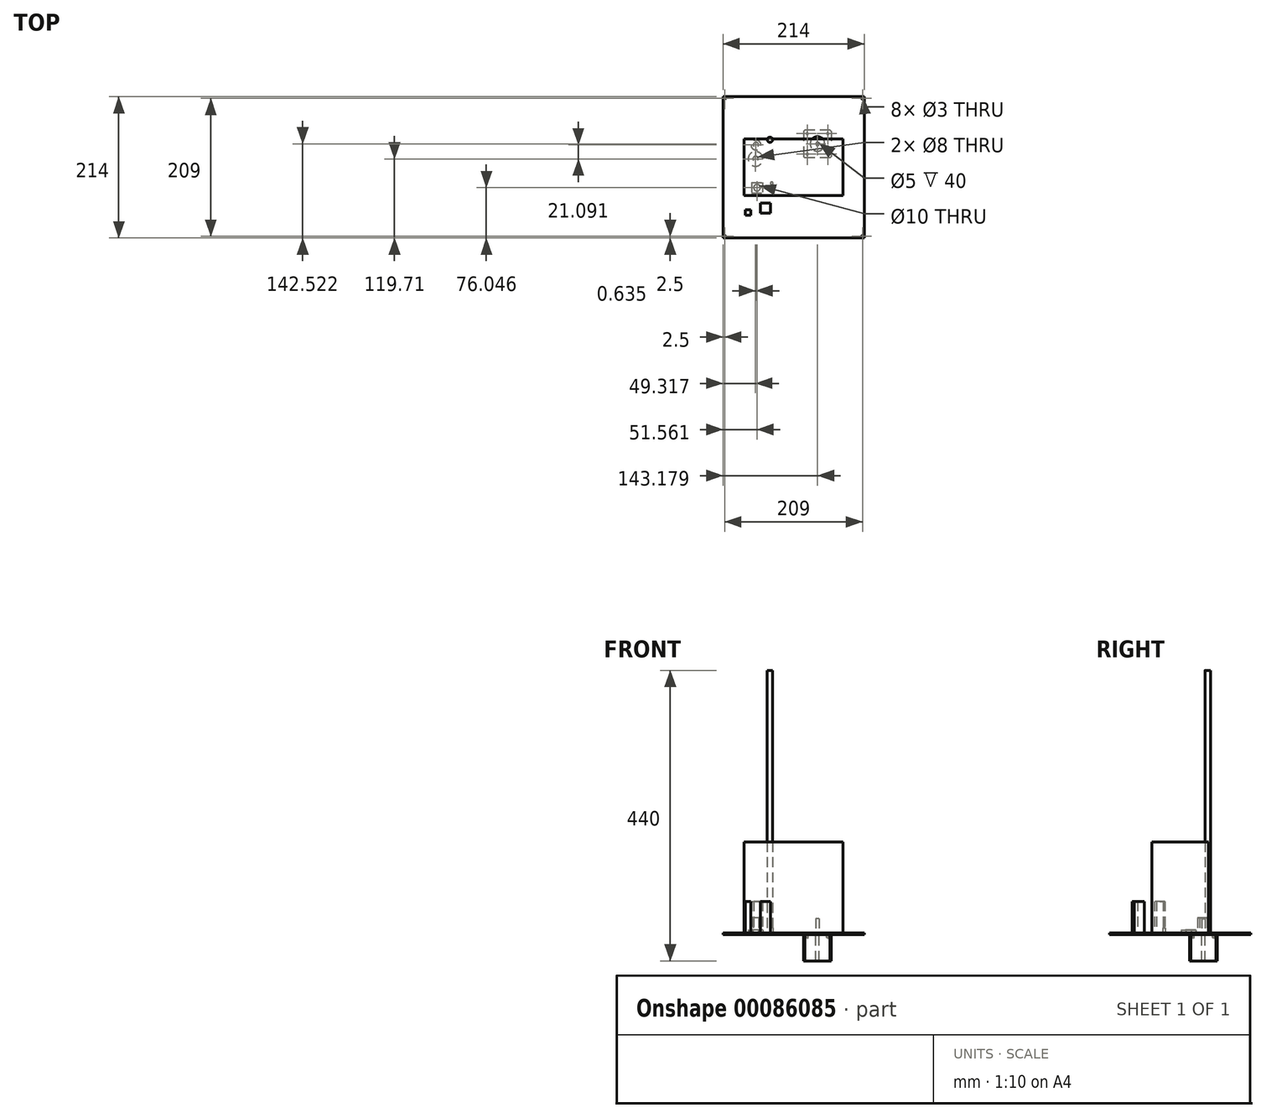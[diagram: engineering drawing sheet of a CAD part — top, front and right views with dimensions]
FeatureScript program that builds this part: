
annotation { "Feature Type Name" : "Feature", "Feature Type Description" : "" }
export const myFeature = defineFeature(function(context is Context, id is Id, definition is map)
    precondition{}
    {
        {
            var Q0;
            Q0=qCreatedBy(makeId("Top.planeOp"),FACE);
            var sketch = newSketch(context, id + "F0", { "sketchPlane" : qUnion([Q0])});
            skCircle(sketch, "E0", {"center": v(-57.05, 33.8) * mm, "radius": 4 * mm});
            skCircle(sketch, "E1", {"center": v(-57.05, 33.8) * mm, "radius": 7.5 * mm});
            skCircle(sketch, "E2", {"center": v(-35.88, 41.78) * mm, "radius": 4 * mm});
            skCircle(sketch, "E3", {"center": v(-57.68, 12.71) * mm, "radius": 11 * mm});
            skCircle(sketch, "E4", {"center": v(-57.68, 12.71) * mm, "radius": 4 * mm});
            skLineSegment(sketch, "E5.bottom", {"start": v(57.18, 56.52) * mm, "end": v(15.18, 56.52) * mm});
            skLineSegment(sketch, "E5.top", {"start": v(57.18, 14.52) * mm, "end": v(15.18, 14.52) * mm});
            skLineSegment(sketch, "E5.left", {"start": v(57.18, 56.52) * mm, "end": v(57.18, 14.52) * mm});
            skLineSegment(sketch, "E5.right", {"start": v(15.18, 56.52) * mm, "end": v(15.18, 14.52) * mm});
            skPoint(sketch, "E5.middle", {"position": v(36.18, 35.52) * mm});
            skCircle(sketch, "E6", {"center": v(36.18, 35.52) * mm, "radius": 11 * mm});
            skCircle(sketch, "E7", {"center": v(36.18, 35.52) * mm, "radius": 2.5 * mm});
            skLineSegment(sketch, "E8", {"start": v(36.18, 56.52) * mm, "end": v(36.18, 14.52) * mm, "construction": true});
            skLineSegment(sketch, "E9", {"start": v(57.18, 35.52) * mm, "end": v(15.18, 35.52) * mm, "construction": true});
            skPoint(sketch, "E10", {"position": v(20.68, 51.02) * mm});
            skPoint(sketch, "E11.MirrorP", {"position": v(51.68, 51.02) * mm});
            skPoint(sketch, "E12.MirrorP", {"position": v(20.68, 20.02) * mm});
            skPoint(sketch, "E13.MirrorP", {"position": v(51.68, 20.02) * mm});
            skLineSegment(sketch, "E14.bottom", {"start": v(-63.44, -22.95) * mm, "end": v(-47.44, -22.95) * mm});
            skLineSegment(sketch, "E14.top", {"start": v(-63.44, -38.95) * mm, "end": v(-47.44, -38.95) * mm});
            skLineSegment(sketch, "E14.left", {"start": v(-63.44, -22.95) * mm, "end": v(-63.44, -38.95) * mm});
            skLineSegment(sketch, "E14.right", {"start": v(-47.44, -22.95) * mm, "end": v(-47.44, -38.95) * mm});
            skPoint(sketch, "E14.middle", {"position": v(-55.44, -30.95) * mm});
            skCircle(sketch, "E15", {"center": v(-33.26, -24.31) * mm, "radius": 2 * mm});
            skLineSegment(sketch, "E16.bottom", {"start": v(-65.2, -64.45) * mm, "end": v(-73.2, -64.45) * mm});
            skLineSegment(sketch, "E16.top", {"start": v(-65.2, -72.45) * mm, "end": v(-73.2, -72.45) * mm});
            skLineSegment(sketch, "E16.left", {"start": v(-65.2, -64.45) * mm, "end": v(-65.2, -72.45) * mm});
            skLineSegment(sketch, "E16.right", {"start": v(-73.2, -64.45) * mm, "end": v(-73.2, -72.45) * mm});
            skPoint(sketch, "E16.middle", {"position": v(-69.2, -68.45) * mm});
            skLineSegment(sketch, "E17.bottom", {"start": v(-50.3, -69.24) * mm, "end": v(-35.3, -69.24) * mm});
            skLineSegment(sketch, "E17.top", {"start": v(-50.3, -54.24) * mm, "end": v(-35.3, -54.24) * mm});
            skLineSegment(sketch, "E17.left", {"start": v(-50.3, -69.24) * mm, "end": v(-50.3, -54.24) * mm});
            skLineSegment(sketch, "E17.right", {"start": v(-35.3, -69.24) * mm, "end": v(-35.3, -54.24) * mm});
            skPoint(sketch, "E17.middle", {"position": v(-42.8, -61.74) * mm});
            skSolve(sketch);
        }
        {
            var Q0;
            Q0=makeQuery(id+"F0.imprint","IMPRINT",FACE,{"disambiguationData":[TD([[makeQuery(id+"F0.imprint","IMPRINT",EDGE,{"derivedFrom":sQuery(id+"F0.wireOp",EDGE,"E0")}),-1.0]])]});
            extrude(context, id + "F1", {"entities" : qUnion([Q0]), "depth" : 25 * mm});
        }
        {
            var Q0;
            Q0=makeQuery(id+"F0.imprint","IMPRINT",FACE,{"disambiguationData":[TD([[makeQuery(id+"F0.imprint","IMPRINT",EDGE,{"derivedFrom":sQuery(id+"F0.wireOp",EDGE,"E2")}),1.0]])]});
            extrude(context, id + "F2", {"entities" : qUnion([Q0]), "depth" : 400 * mm});
        }
        {
            var Q0;
            Q0=makeQuery(id+"F0.imprint","IMPRINT",FACE,{"disambiguationData":[TD([[makeQuery(id+"F0.imprint","IMPRINT",EDGE,{"derivedFrom":sQuery(id+"F0.wireOp",EDGE,"E3")}),1.0]])]});
            extrude(context, id + "F3", {"entities" : qUnion([Q0]), "depth" : 7 * mm});
        }
        {
            var Q0;
            Q0=makeQuery(id+"F3.opExtrude","CAP_EDGE",EDGE,{"disambiguationData":[OSD([sQuery(id+"F0.wireOp",EDGE,"E3")])],"isStart":false});
            var Q1;
            Q1=makeQuery(id+"F3.opExtrude","CAP_EDGE",EDGE,{"disambiguationData":[OSD([sQuery(id+"F0.wireOp",EDGE,"E4")])],"isStart":false});
            var Q2;
            Q2=makeQuery(id+"F3.opExtrude","CAP_EDGE",EDGE,{"disambiguationData":[OSD([sQuery(id+"F0.wireOp",EDGE,"E4")])],"isStart":true});
            var Q3;
            Q3=makeQuery(id+"F3.opExtrude","CAP_EDGE",EDGE,{"disambiguationData":[OSD([sQuery(id+"F0.wireOp",EDGE,"E3")])],"isStart":true});
            fillet(context, id + "F4", {"entities" : qUnion([Q0, Q1, Q2, Q3]), "radius" : 0.5 * mm, "tangentPropagation" : true, "allowEdgeOverflow" : false});
        }
        {
            var Q0;
            Q0=makeQuery(id+"F0.imprint","IMPRINT",FACE,{"disambiguationData":[TD([[makeQuery(id+"F0.imprint","IMPRINT",EDGE,{"derivedFrom":sQuery(id+"F0.wireOp",EDGE,"E5.bottom")}),1.0]])]});
            var Q1;
            Q1=makeQuery(id+"F0.imprint","IMPRINT",FACE,{"disambiguationData":[TD([[makeQuery(id+"F0.imprint","IMPRINT",EDGE,{"derivedFrom":sQuery(id+"F0.wireOp",EDGE,"E6")}),1.0]])]});
            extrude(context, id + "F5", {"entities" : qUnion([Q0, Q1]), "oppositeDirection" : true, "depth" : 40 * mm});
        }
        {
            var Q0;
            Q0=makeQuery(id+"F0.imprint","IMPRINT",FACE,{"disambiguationData":[TD([[makeQuery(id+"F0.imprint","IMPRINT",EDGE,{"derivedFrom":sQuery(id+"F0.wireOp",EDGE,"E6")}),1.0]])]});
            extrude(context, id + "F6", {"entities" : qUnion([Q0]), "operationType" : NewBodyOperationType.ADD, "depth" : 2 * mm});
        }
        {
            var Q0;
            Q0=makeQuery(id+"F0.imprint","IMPRINT",FACE,{"disambiguationData":[TD([[makeQuery(id+"F0.imprint","IMPRINT",EDGE,{"derivedFrom":sQuery(id+"F0.wireOp",EDGE,"E7")}),1.0]])]});
            extrude(context, id + "F7", {"entities" : qUnion([Q0]), "operationType" : NewBodyOperationType.ADD, "depth" : 24 * mm});
        }
        {
            var Q0;
            Q0=makeQuery(id+"F5.opExtrude","SWEPT_EDGE",EDGE,{"disambiguationData":[OSD([sQuery(id+"F0.wireOp",EDGE,"E5.bottom"),sQuery(id+"F0.wireOp",EDGE,"E5.left")])]});
            var Q1;
            Q1=makeQuery(id+"F5.opExtrude","SWEPT_EDGE",EDGE,{"disambiguationData":[OSD([sQuery(id+"F0.wireOp",EDGE,"E5.bottom"),sQuery(id+"F0.wireOp",EDGE,"E5.right")])]});
            var Q2;
            Q2=makeQuery(id+"F5.opExtrude","SWEPT_EDGE",EDGE,{"disambiguationData":[OSD([sQuery(id+"F0.wireOp",EDGE,"E5.top"),sQuery(id+"F0.wireOp",EDGE,"E5.right")])]});
            var Q3;
            Q3=makeQuery(id+"F5.opExtrude","SWEPT_EDGE",EDGE,{"disambiguationData":[OSD([sQuery(id+"F0.wireOp",EDGE,"E5.top"),sQuery(id+"F0.wireOp",EDGE,"E5.left")])]});
            chamfer(context, id + "F8", {"entities" : qUnion([Q0, Q1, Q2, Q3]), "width" : 2 * mm, "tangentPropagation" : true});
        }
        {
            var Q0;
            Q0=sQuery(id+"F0.wireOp",VERTEX,"E10");
            var Q1;
            Q1=sQuery(id+"F0.wireOp",VERTEX,"E11.MirrorP");
            var Q2;
            Q2=sQuery(id+"F0.wireOp",VERTEX,"E13.MirrorP");
            var Q3;
            Q3=sQuery(id+"F0.wireOp",VERTEX,"E12.MirrorP");
            var Q4;
            Q4=makeQuery(id+"F5.opExtrude","SWEPT_BODY",BODY,{"disambiguationData":[OSD([sQuery(id+"F0.wireOp",EDGE,"E5.bottom"),sQuery(id+"F0.wireOp",EDGE,"E5.top"),sQuery(id+"F0.wireOp",EDGE,"E5.left"),sQuery(id+"F0.wireOp",EDGE,"E5.right"),sQuery(id+"F0.wireOp",EDGE,"E7")])]});
            hole(context, id + "F9", {"style" : HoleStyle.SIMPLE, "endStyle" : HoleEndStyle.BLIND, "holeDiameter" : 3 * mm, "holeDepth" : 5 * mm, "locations" : qUnion([Q0, Q1, Q2, Q3]), "scope" : qUnion([Q4])});
        }
        {
            var Q0;
            Q0=qCreatedBy(makeId("Top.planeOp"),FACE);
            var sketch = newSketch(context, id + "F10", { "sketchPlane" : qUnion([Q0])});
            skLineSegment(sketch, "E18.bottom", {"start": v(-107, 107) * mm, "end": v(107, 107) * mm});
            skLineSegment(sketch, "E18.top", {"start": v(-107, -107) * mm, "end": v(107, -107) * mm});
            skLineSegment(sketch, "E18.left", {"start": v(-107, 107) * mm, "end": v(-107, -107) * mm});
            skLineSegment(sketch, "E18.right", {"start": v(107, 107) * mm, "end": v(107, -107) * mm});
            skPoint(sketch, "E18.middle", {"position": v(0, 0) * mm});
            skLineSegment(sketch, "E19.bottom", {"start": v(-104.5, 104.5) * mm, "end": v(104.5, 104.5) * mm, "construction": true});
            skLineSegment(sketch, "E19.top", {"start": v(-104.5, -104.5) * mm, "end": v(104.5, -104.5) * mm, "construction": true});
            skLineSegment(sketch, "E19.left", {"start": v(-104.5, 104.5) * mm, "end": v(-104.5, -104.5) * mm, "construction": true});
            skLineSegment(sketch, "E19.right", {"start": v(104.5, 104.5) * mm, "end": v(104.5, -104.5) * mm, "construction": true});
            skPoint(sketch, "E20", {"position": v(-104.5, 104.5) * mm});
            skPoint(sketch, "E21", {"position": v(104.5, 104.5) * mm});
            skPoint(sketch, "E22", {"position": v(-104.5, -104.5) * mm});
            skPoint(sketch, "E23", {"position": v(104.5, -104.5) * mm});
            skSolve(sketch);
        }
        {
            var Q0;
            Q0=makeQuery(id+"F10.imprint","IMPRINT",FACE,{"disambiguationData":[TD([[makeQuery(id+"F10.imprint","IMPRINT",EDGE,{"derivedFrom":sQuery(id+"F10.wireOp",EDGE,"E18.bottom")}),-1.0]])]});
            extrude(context, id + "F11", {"entities" : qUnion([Q0]), "depth" : 2 * mm});
        }
        {
            var Q0;
            Q0=sQuery(id+"F10.wireOp",VERTEX,"E20");
            var Q1;
            Q1=sQuery(id+"F10.wireOp",VERTEX,"E21");
            var Q2;
            Q2=sQuery(id+"F10.wireOp",VERTEX,"E23");
            var Q3;
            Q3=sQuery(id+"F10.wireOp",VERTEX,"E22");
            var Q4;
            Q4=makeQuery(id+"F11.opExtrude","SWEPT_BODY",BODY,{"disambiguationData":[OSD([sQuery(id+"F10.wireOp",EDGE,"E18.bottom"),sQuery(id+"F10.wireOp",EDGE,"E18.top"),sQuery(id+"F10.wireOp",EDGE,"E18.left"),sQuery(id+"F10.wireOp",EDGE,"E18.right")])]});
            hole(context, id + "F12", {"style" : HoleStyle.SIMPLE, "endStyle" : HoleEndStyle.THROUGH, "oppositeDirection" : true, "holeDiameter" : 3 * mm, "locations" : qUnion([Q0, Q1, Q2, Q3]), "scope" : qUnion([Q4]), "isTappedThrough" : true});
        }
        {
            var Q0;
            Q0=qCreatedBy(makeId("Top.planeOp"),FACE);
            var sketch = newSketch(context, id + "F13", { "sketchPlane" : qUnion([Q0])});
            skLineSegment(sketch, "E24.bottom", {"start": v(-75, 43) * mm, "end": v(75, 43) * mm});
            skLineSegment(sketch, "E24.top", {"start": v(-75, -43) * mm, "end": v(75, -43) * mm});
            skLineSegment(sketch, "E24.left", {"start": v(-75, 43) * mm, "end": v(-75, -43) * mm});
            skLineSegment(sketch, "E24.right", {"start": v(75, 43) * mm, "end": v(75, -43) * mm});
            skPoint(sketch, "E24.middle", {"position": v(0, 0) * mm});
            skSolve(sketch);
        }
        {
            var Q0;
            Q0=makeQuery(id+"F13.imprint","IMPRINT",FACE,{"disambiguationData":[TD([[makeQuery(id+"F13.imprint","IMPRINT",EDGE,{"derivedFrom":sQuery(id+"F13.wireOp",EDGE,"E24.bottom")}),-1.0]])]});
            extrude(context, id + "F14", {"entities" : qUnion([Q0]), "depth" : 140 * mm});
        }
        {
            var Q0;
            Q0=makeQuery(id+"F0.imprint","IMPRINT",FACE,{"disambiguationData":[TD([[makeQuery(id+"F0.imprint","IMPRINT",EDGE,{"derivedFrom":sQuery(id+"F0.wireOp",EDGE,"E14.bottom")}),-1.0]])]});
            extrude(context, id + "F15", {"entities" : qUnion([Q0]), "depth" : 50 * mm});
        }
        {
            var Q0;
            Q0=sQuery(id+"F0.wireOp",VERTEX,"E14.middle");
            var Q1;
            Q1=makeQuery(id+"F15.opExtrude","SWEPT_BODY",BODY,{"disambiguationData":[OSD([sQuery(id+"F0.wireOp",EDGE,"E14.bottom"),sQuery(id+"F0.wireOp",EDGE,"E14.top"),sQuery(id+"F0.wireOp",EDGE,"E14.left"),sQuery(id+"F0.wireOp",EDGE,"E14.right")])]});
            hole(context, id + "F16", {"style" : HoleStyle.SIMPLE, "endStyle" : HoleEndStyle.THROUGH, "oppositeDirection" : true, "holeDiameter" : 10 * mm, "locations" : qUnion([Q0]), "scope" : qUnion([Q1]), "isTappedThrough" : true});
        }
        {
            var Q0;
            Q0=makeQuery(id+"F0.imprint","IMPRINT",FACE,{"disambiguationData":[TD([[makeQuery(id+"F0.imprint","IMPRINT",EDGE,{"derivedFrom":sQuery(id+"F0.wireOp",EDGE,"E15")}),1.0]])]});
            extrude(context, id + "F17", {"entities" : qUnion([Q0]), "depth" : 10 * mm});
        }
        {
            var Q0;
            Q0=makeQuery(id+"F0.imprint","IMPRINT",FACE,{"disambiguationData":[TD([[makeQuery(id+"F0.imprint","IMPRINT",EDGE,{"derivedFrom":sQuery(id+"F0.wireOp",EDGE,"E16.bottom")}),1.0]])]});
            extrude(context, id + "F18", {"entities" : qUnion([Q0]), "depth" : 50 * mm});
        }
        {
            var Q0;
            Q0=makeQuery(id+"F0.imprint","IMPRINT",FACE,{"disambiguationData":[TD([[makeQuery(id+"F0.imprint","IMPRINT",EDGE,{"derivedFrom":sQuery(id+"F0.wireOp",EDGE,"E17.bottom")}),1.0]])]});
            extrude(context, id + "F19", {"entities" : qUnion([Q0]), "depth" : 50 * mm});
        }
    });
